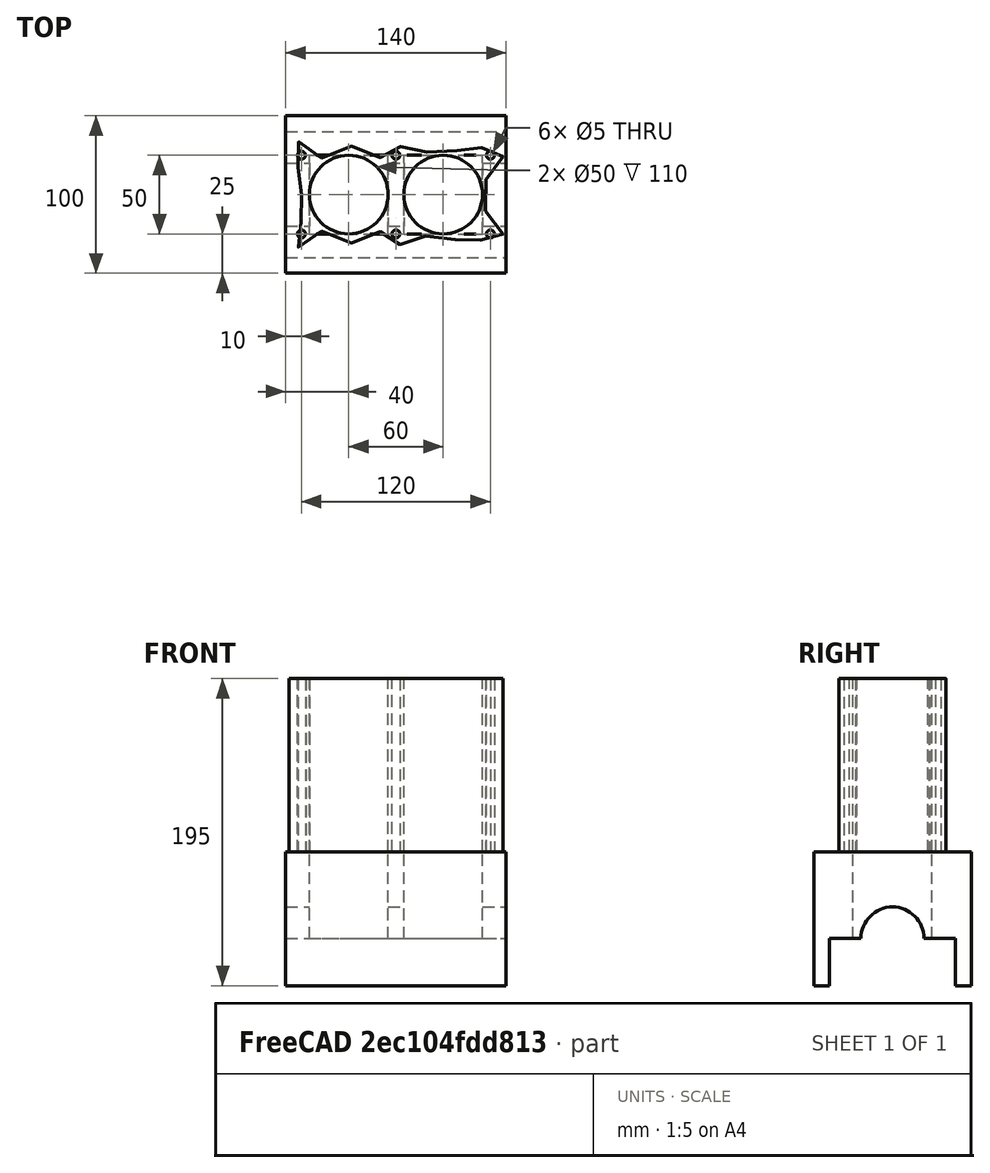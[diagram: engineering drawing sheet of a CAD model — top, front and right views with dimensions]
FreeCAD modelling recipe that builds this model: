
FCSTD DOCUMENT  (FreeCAD 0.19R17171 (Git))
Label: EngineBlock
License: CC-BY 3.0
LicenseURL: http://creativecommons.org/licenses/by/3.0/
objects: Part::Part2DObjectPython×8, Part::Extrusion×7, Part::Box×5, Part::Cut×5, Part::Cylinder×3, Part::MultiFuse×3, Part::Mirroring×3, App::DocumentObjectGroup×1, Part::MultiCommon×1
note: 35 computed .brp shape members not serialized (recipe doc carries the construction recipe); baked Part::Feature solids carry a one-line shape summary decoded from their .brp

FEATURE [Part::Box] Box  label="Billet"
  AttacherType = Attacher::AttachEngine3D
  Height = 110
  Length = 140
  Placement = pos=(0,-40,0) rot=(0,0,1;0rad)
  Width = 80
FEATURE [Part::Cylinder] Cylinder  label="Cylinder 1"
  Angle = 360
  AttacherType = Attacher::AttachEngine3D
  Height = 110
  Placement = pos=(40,0,0) rot=(0,0,1;0rad)
  Radius = 25
FEATURE [Part::Cylinder] Cylinder001  label="Cylinder 2"
  Angle = 360
  AttacherType = Attacher::AttachEngine3D
  Height = 110
  Placement = pos=(100,0,0) rot=(0,0,1;0rad)
  Radius = 25
FEATURE [Part::MultiFuse] Fusion  label="Cylinders"
  Shapes = -> [Cylinder,Cylinder001]
FEATURE [Part::Cut] Cut  label="Bored Block"
  Base = -> Box
  Tool = -> Fusion
FEATURE [Part::Box] Box001  label="Crankcase Billet"
  AttacherType = Attacher::AttachEngine3D
  Height = 85
  Length = 140
  Placement = pos=(0,-50,-85) rot=(0,0,1;0rad)
  Width = 100
FEATURE [Part::Box] Box002  label="Bearing carve"
  AttacherType = Attacher::AttachEngine3D
  Height = 30
  Length = 140
  Placement = pos=(0,-40,-85) rot=(0,0,1;0rad)
  Width = 80
FEATURE [Part::Cut] Cut001  label="Carved crankcase"
  Base = -> Box001
  Tool = -> Box002
FEATURE [Part::Cylinder] Cylinder002  label="Cranshaft carve"
  Angle = 360
  AttacherType = Attacher::AttachEngine3D
  Height = 140
  Placement = pos=(0,0,-55) rot=(0,1,0;1.5708rad)
  Radius = 20
FEATURE [Part::Cut] Cut002  label="Crankcase with journals"
  Base = -> Cut001
  Tool = -> Cylinder002
FEATURE [Part::Box] Box003  label="Box carve 1"
  AttacherType = Attacher::AttachEngine3D
  Height = 55
  Length = 50
  Placement = pos=(15,-25,-55) rot=(0,0,1;0rad)
  Width = 50
FEATURE [Part::Box] Box004  label="Box carve 2"
  AttacherType = Attacher::AttachEngine3D
  Height = 55
  Length = 50
  Placement = pos=(75,-25,-55) rot=(0,0,1;0rad)
  Width = 50
FEATURE [Part::MultiFuse] Fusion001  label="Box carvers"
  Shapes = -> [Box003,Box004]
FEATURE [Part::Cut] Cut003  label="Crankcase"
  Base = -> Cut002
  Tool = -> Fusion001
FEATURE [Part::Part2DObjectPython] Circle003  label="Bolt 007"  # Draft 2D object (typed FeaturePython)
  FirstAngle = 0
  LastAngle = 0
  MapMode = 5
  Placement = pos=(10,25,110) rot=(0,0,1;0rad)
  Radius = 2.5
FEATURE [Part::Mirroring] Part__Mirroring  label="Bolt 4"
  Base = (0,0,0)
  Normal = (0,1,0)
  Source = -> Circle003
FEATURE [Part::Extrusion] Extrude  label="Head bolt bore 1"
  Base = -> Circle003
  Dir = (0,0,-110)
  DirMode = 0
  FaceMakerClass = Part::FaceMakerExtrusion
  LengthFwd = 0
  LengthRev = 0
  Solid = false
  Symmetric = false
FEATURE [Part::Extrusion] Extrude003  label="Head bolt bore 4"
  Base = -> Part__Mirroring
  Dir = (0,0,-110)
  DirMode = 0
  FaceMakerClass = Part::FaceMakerExtrusion
  LengthFwd = 0
  LengthRev = 0
  Solid = false
  Symmetric = false
FEATURE [Part::Part2DObjectPython] Circle004  label="Bolt 008"  # Draft 2D object (typed FeaturePython)
  FirstAngle = 0
  LastAngle = 0
  MapMode = 5
  Placement = pos=(70,25,110) rot=(0,0,1;0rad)
  Radius = 2.5
FEATURE [Part::Mirroring] Part__Mirroring001  label="Bolt 5"
  Base = (0,0,0)
  Normal = (0,1,0)
  Source = -> Circle004
FEATURE [Part::Extrusion] Extrude001  label="Head bolt bore 2"
  Base = -> Circle004
  Dir = (0,0,-110)
  DirMode = 0
  FaceMakerClass = Part::FaceMakerExtrusion
  LengthFwd = 0
  LengthRev = 0
  Solid = false
  Symmetric = false
FEATURE [Part::Extrusion] Extrude004  label="Head bolt bore 5"
  Base = -> Part__Mirroring001
  Dir = (0,0,-110)
  DirMode = 0
  FaceMakerClass = Part::FaceMakerExtrusion
  LengthFwd = 0
  LengthRev = 0
  Solid = false
  Symmetric = false
FEATURE [Part::Part2DObjectPython] Circle005  label="Bolt 009"  # Draft 2D object (typed FeaturePython)
  FirstAngle = 0
  LastAngle = 0
  MapMode = 5
  Placement = pos=(130,25,110) rot=(0,0,1;0rad)
  Radius = 2.5
FEATURE [Part::Mirroring] Part__Mirroring002  label="Bolt 6"
  Base = (0,0,0)
  Normal = (0,1,0)
  Source = -> Circle005
FEATURE [Part::Extrusion] Extrude002  label="Head bolt bore 3"
  Base = -> Circle005
  Dir = (0,0,-110)
  DirMode = 0
  FaceMakerClass = Part::FaceMakerExtrusion
  LengthFwd = 0
  LengthRev = 0
  Solid = false
  Symmetric = false
FEATURE [Part::Extrusion] Extrude005  label="Head bolt bore 6"
  Base = -> Part__Mirroring002
  Dir = (0,0,-110)
  DirMode = 0
  FaceMakerClass = Part::FaceMakerExtrusion
  LengthFwd = 0
  LengthRev = 0
  Solid = false
  Symmetric = false
FEATURE [Part::MultiFuse] Fusion002  label="Head bolt boreholes"
  Shapes = -> [Extrude,Extrude001,Extrude002,Extrude003,Extrude004,Extrude005]
FEATURE [Part::Cut] Cut004  label="Block with headbolts"
  Base = -> Cut
  Tool = -> Fusion002
FEATURE [Part::Part2DObjectPython] Polygon004  # Draft 2D object (typed FeaturePython)
  ChamferSize = 0
  DrawMode = 0
  FacesNumber = 14
  FilletRadius = 0
  MapMode = 5
  Placement = pos=(40,0,110) rot=(0,0,1;0rad)
  Radius = 30
FEATURE [Part::Part2DObjectPython] Polygon005  # Draft 2D object (typed FeaturePython)
  ChamferSize = 0
  DrawMode = 0
  FacesNumber = 14
  FilletRadius = 0
  MapMode = 5
  Placement = pos=(100,0,110) rot=(0,0,1;0rad)
  Radius = 30
FEATURE [Part::Part2DObjectPython] Polygon006  # Draft 2D object (typed FeaturePython)
  ChamferSize = 0
  DrawMode = 0
  FacesNumber = 22
  FilletRadius = 0
  MapMode = 5
  Placement = pos=(40,0,110) rot=(0,0,1;0rad)
  Radius = 45
FEATURE [Part::Part2DObjectPython] Polygon007  # Draft 2D object (typed FeaturePython)
  ChamferSize = 0
  DrawMode = 0
  FacesNumber = 22
  FilletRadius = 0
  MapMode = 5
  Placement = pos=(100,0,110) rot=(0,0,1;0rad)
  Radius = 45
FEATURE [App::DocumentObjectGroup] Construction
  Group = -> [Polygon004,Polygon005,Polygon006,Polygon007]
FEATURE [Part::Part2DObjectPython] BSpline001  # Draft 2D object (typed FeaturePython)
  Closed = true
  MapMode = 5
  Points = (36) [(1.74614e-119,4133350,123145000000000),(625142000,802825,123145000000000),(463715000,11434000000,123145000000000),+33 more]
FEATURE [Part::Extrusion] Extrude006  label="Extruded spline"
  Base = -> BSpline001
  Dir = (0,0,-110)
  DirMode = 0
  FaceMakerClass = Part::FaceMakerExtrusion
  LengthFwd = 0
  LengthRev = 0
  Solid = false
  Symmetric = false
FEATURE [Part::MultiCommon] Common  label="Engine block"
  Shapes = -> [Extrude006,Cut004]
